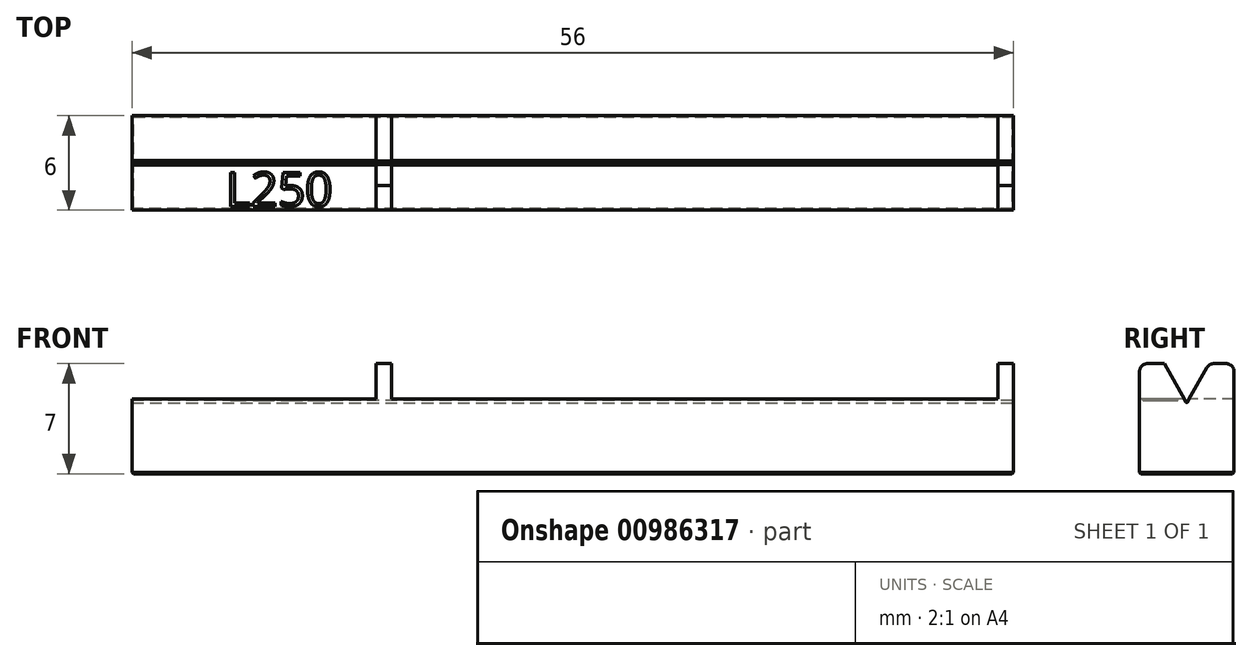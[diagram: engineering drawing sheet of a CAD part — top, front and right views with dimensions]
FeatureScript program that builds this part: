
annotation { "Feature Type Name" : "Feature", "Feature Type Description" : "" }
export const myFeature = defineFeature(function(context is Context, id is Id, definition is map)
    precondition{}
    {
        {
            var Q0;
            Q0=qCreatedBy(makeId("Top.planeOp"),FACE);
            var sketch = newSketch(context, id + "F0", { "sketchPlane" : qUnion([Q0])});
            skLineSegment(sketch, "E0.bottom", {"start": v(-28, 3) * mm, "end": v(28, 3) * mm});
            skLineSegment(sketch, "E0.top", {"start": v(-28, -3) * mm, "end": v(28, -3) * mm});
            skLineSegment(sketch, "E0.left", {"start": v(-28, 3) * mm, "end": v(-28, -3) * mm});
            skLineSegment(sketch, "E0.right", {"start": v(28, 3) * mm, "end": v(28, -3) * mm});
            skLineSegment(sketch, "E1", {"start": v(0, 9.05) * mm, "end": v(0, -9.2) * mm, "construction": true});
            skLineSegment(sketch, "E2", {"start": v(-9.84, 0) * mm, "end": v(11.26, 0) * mm, "construction": true});
            skSolve(sketch);
        }
        {
            var Q0;
            Q0 = qSketchRegion(id + "F0", true);
            extrude(context, id + "F1", {"entities" : qUnion([Q0]), "depth" : 7 * mm, "offsetDistance" : 25 * mm});
        }
        {
            var Q0;
            Q0=makeQuery(id+"F1.opExtrude","CAP_FACE",FACE,{"disambiguationData":[OSD([sQuery(id+"F0.wireOp",EDGE,"E0.bottom"),sQuery(id+"F0.wireOp",EDGE,"E0.top"),sQuery(id+"F0.wireOp",EDGE,"E0.left"),sQuery(id+"F0.wireOp",EDGE,"E0.right")])],"isStart":false});
            var sketch = newSketch(context, id + "F2", { "sketchPlane" : qUnion([Q0])});
            skLineSegment(sketch, "E3.bottom", {"start": v(-11.5, -3) * mm, "end": v(27, -3) * mm});
            skLineSegment(sketch, "E3.top", {"start": v(-11.5, 3) * mm, "end": v(27, 3) * mm});
            skLineSegment(sketch, "E3.left", {"start": v(-11.5, -3) * mm, "end": v(-11.5, 3) * mm});
            skLineSegment(sketch, "E3.right", {"start": v(27, -3) * mm, "end": v(27, 3) * mm});
            skLineSegment(sketch, "E4.bottom", {"start": v(-28, -3) * mm, "end": v(-12.5, -3) * mm});
            skLineSegment(sketch, "E4.top", {"start": v(-28, 3) * mm, "end": v(-12.5, 3) * mm});
            skLineSegment(sketch, "E4.left", {"start": v(-28, -3) * mm, "end": v(-28, 3) * mm});
            skLineSegment(sketch, "E4.right", {"start": v(-12.5, -3) * mm, "end": v(-12.5, 3) * mm});
            skSolve(sketch);
        }
        {
            var Q0;
            Q0 = qSketchRegion(id + "F2", true);
            extrude(context, id + "F3", {"entities" : qUnion([Q0]), "operationType" : NewBodyOperationType.REMOVE, "oppositeDirection" : true, "depth" : (7 - 4.76) * mm, "offsetDistance" : 25 * mm});
        }
        {
            var Q0;
            Q0=makeQuery(id+"F1.opExtrude","SWEPT_FACE",FACE,{"disambiguationData":[OSD([sQuery(id+"F0.wireOp",EDGE,"E0.right")])]});
            var sketch = newSketch(context, id + "F4", { "sketchPlane" : qUnion([Q0])});
            skLineSegment(sketch, "E5", {"start": v(-1.44, 7) * mm, "end": v(-0.1, 4.7) * mm});
            skLineSegment(sketch, "E6", {"start": v(1.44, 7) * mm, "end": v(-1.44, 7) * mm});
            skArc(sketch, "E7", {"start": v(-0.05, 4.55) * mm, "mid": v(0, 4.52) * mm, "end": v(0.05, 4.55) * mm});
            skLineSegment(sketch, "E8", {"start": v(-0.1, 4.7) * mm, "end": v(-0.05, 4.55) * mm});
            skLineSegment(sketch, "E9", {"start": v(0.05, 4.55) * mm, "end": v(0.1, 4.7) * mm});
            skLineSegment(sketch, "E10.trimOffspring", {"start": v(0.1, 4.7) * mm, "end": v(1.44, 7) * mm});
            skLineSegment(sketch, "E11", {"start": v(0, 7) * mm, "end": v(0, -0.68) * mm, "construction": true});
            skLineSegment(sketch, "E12", {"start": v(-0.05, 4.55) * mm, "end": v(0, 4.44) * mm, "construction": true});
            skLineSegment(sketch, "E13", {"start": v(0, 4.44) * mm, "end": v(0.05, 4.55) * mm, "construction": true});
            skSolve(sketch);
        }
        {
            var Q0;
            Q0 = qSketchRegion(id + "F4", true);
            extrude(context, id + "F5", {"entities" : qUnion([Q0]), "operationType" : NewBodyOperationType.REMOVE, "endBound" : BoundingType.THROUGH_ALL, "oppositeDirection" : true, "depth" : 25 * mm, "offsetDistance" : 25 * mm});
        }
        {
            var Q0;
            {var subQ0=sQuery(id+"F0.wireOp",EDGE,"E0.right");var subQ1=sQuery(id+"F0.wireOp",EDGE,"E0.top");Q0=makeQuery(id+"F3.boolean.opBoolean","SPLIT",EDGE,{"disambiguationData":[TD([makeQuery(id+"F1.opExtrude","SWEPT_FACE",FACE,{"disambiguationData":[OSD([subQ0])]})])],"derivedFrom":makeQuery(id+"F1.opExtrude","CAP_EDGE",EDGE,{"disambiguationData":[OSD([subQ1])],"isStart":false})});}
            var Q1;
            {var subQ0=sQuery(id+"F0.wireOp",EDGE,"E0.bottom");var subQ1=sQuery(id+"F0.wireOp",EDGE,"E0.right");Q1=makeQuery(id+"F3.boolean.opBoolean","SPLIT",EDGE,{"disambiguationData":[TD([makeQuery(id+"F1.opExtrude","SWEPT_FACE",FACE,{"disambiguationData":[OSD([subQ1])]})])],"derivedFrom":makeQuery(id+"F1.opExtrude","CAP_EDGE",EDGE,{"disambiguationData":[OSD([subQ0])],"isStart":false})});}
            var Q2;
            {var subQ0=sQuery(id+"F0.wireOp",EDGE,"E0.top");Q2=makeQuery(id+"F3.boolean.opBoolean","SPLIT",EDGE,{"disambiguationData":[TD([makeQuery(id+"F3.opExtrude","SWEPT_FACE",FACE,{"disambiguationData":[OSD([sQuery(id+"F2.wireOp",EDGE,"E3.left")])]})])],"derivedFrom":makeQuery(id+"F1.opExtrude","CAP_EDGE",EDGE,{"disambiguationData":[OSD([subQ0])],"isStart":false})});}
            var Q3;
            {var subQ0=sQuery(id+"F0.wireOp",EDGE,"E0.bottom");Q3=makeQuery(id+"F3.boolean.opBoolean","SPLIT",EDGE,{"disambiguationData":[TD([makeQuery(id+"F3.opExtrude","SWEPT_FACE",FACE,{"disambiguationData":[OSD([sQuery(id+"F2.wireOp",EDGE,"E3.left")])]})])],"derivedFrom":makeQuery(id+"F1.opExtrude","CAP_EDGE",EDGE,{"disambiguationData":[OSD([subQ0])],"isStart":false})});}
            var Q4;
            {var subQ0=sQuery(id+"F0.wireOp",EDGE,"E0.right");var subQ1=sQuery(id+"F4.wireOp",EDGE,"E10.trimOffspring");Q4=makeQuery(id+"F5.boolean.opBoolean","COPY",EDGE,{"disambiguationData":[TD([makeQuery(id+"F3.boolean.opBoolean","COPY",FACE,{"derivedFrom":makeQuery(id+"F3.opExtrude","SWEPT_FACE",FACE,{"disambiguationData":[OSD([sQuery(id+"F2.wireOp",EDGE,"E3.left")])]})})])],"derivedFrom":makeQuery(id+"F5.opExtrude","SWEPT_EDGE",EDGE,{"disambiguationData":[OSD([subQ0,sQuery(id+"F4.wireOp",EDGE,"E6"),subQ1])]})});}
            var Q5;
            {var subQ0=sQuery(id+"F0.wireOp",EDGE,"E0.right");var subQ1=sQuery(id+"F4.wireOp",EDGE,"E5");Q5=makeQuery(id+"F5.boolean.opBoolean","COPY",EDGE,{"disambiguationData":[TD([makeQuery(id+"F3.boolean.opBoolean","COPY",FACE,{"derivedFrom":makeQuery(id+"F3.opExtrude","SWEPT_FACE",FACE,{"disambiguationData":[OSD([sQuery(id+"F2.wireOp",EDGE,"E3.left")])]})})])],"derivedFrom":makeQuery(id+"F5.opExtrude","SWEPT_EDGE",EDGE,{"disambiguationData":[OSD([subQ0,subQ1,sQuery(id+"F4.wireOp",EDGE,"E6")])]})});}
            var Q6;
            {var subQ0=sQuery(id+"F0.wireOp",EDGE,"E0.right");var subQ1=sQuery(id+"F4.wireOp",EDGE,"E5");Q6=makeQuery(id+"F5.boolean.opBoolean","COPY",EDGE,{"disambiguationData":[TD([makeQuery(id+"F1.opExtrude","SWEPT_FACE",FACE,{"disambiguationData":[OSD([subQ0])]})])],"derivedFrom":makeQuery(id+"F5.opExtrude","SWEPT_EDGE",EDGE,{"disambiguationData":[OSD([subQ0,subQ1,sQuery(id+"F4.wireOp",EDGE,"E6")])]})});}
            var Q7;
            {var subQ0=sQuery(id+"F0.wireOp",EDGE,"E0.right");var subQ1=sQuery(id+"F4.wireOp",EDGE,"E10.trimOffspring");Q7=makeQuery(id+"F5.boolean.opBoolean","COPY",EDGE,{"disambiguationData":[TD([makeQuery(id+"F1.opExtrude","SWEPT_FACE",FACE,{"disambiguationData":[OSD([subQ0])]})])],"derivedFrom":makeQuery(id+"F5.opExtrude","SWEPT_EDGE",EDGE,{"disambiguationData":[OSD([subQ0,sQuery(id+"F4.wireOp",EDGE,"E6"),subQ1])]})});}
            fillet(context, id + "F6", {"entities" : qUnion([Q0, Q1, Q2, Q3, Q4, Q5, Q6, Q7]), "radius" : 0.5 * mm, "tangentPropagation" : true, "allowEdgeOverflow" : false});
        }
        {
            var Q0;
            Q0=makeQuery(id+"F1.opExtrude","CAP_EDGE",EDGE,{"disambiguationData":[OSD([sQuery(id+"F0.wireOp",EDGE,"E0.top")])],"isStart":true});
            var Q1;
            Q1=makeQuery(id+"F1.opExtrude","CAP_EDGE",EDGE,{"disambiguationData":[OSD([sQuery(id+"F0.wireOp",EDGE,"E0.right")])],"isStart":true});
            var Q2;
            Q2=makeQuery(id+"F1.opExtrude","CAP_EDGE",EDGE,{"disambiguationData":[OSD([sQuery(id+"F0.wireOp",EDGE,"E0.bottom")])],"isStart":true});
            var Q3;
            Q3=makeQuery(id+"F1.opExtrude","CAP_EDGE",EDGE,{"disambiguationData":[OSD([sQuery(id+"F0.wireOp",EDGE,"E0.left")])],"isStart":true});
            var Q4;
            {var subQ0=sQuery(id+"F2.wireOp",EDGE,"E4.left");Q4=makeQuery(id+"F5.boolean.opBoolean","SPLIT",EDGE,{"disambiguationData":[TD([makeQuery(id+"F1.opExtrude","SWEPT_FACE",FACE,{"disambiguationData":[OSD([sQuery(id+"F0.wireOp",EDGE,"E0.top")])]})])],"derivedFrom":makeQuery(id+"F3.boolean.opBoolean","COPY",EDGE,{"derivedFrom":makeQuery(id+"F3.opExtrude","CAP_EDGE",EDGE,{"disambiguationData":[OSD([subQ0])],"isStart":false})})});}
            var Q5;
            {var subQ0=sQuery(id+"F2.wireOp",EDGE,"E4.left");Q5=makeQuery(id+"F5.boolean.opBoolean","SPLIT",EDGE,{"disambiguationData":[TD([makeQuery(id+"F1.opExtrude","SWEPT_FACE",FACE,{"disambiguationData":[OSD([sQuery(id+"F0.wireOp",EDGE,"E0.bottom")])]})])],"derivedFrom":makeQuery(id+"F3.boolean.opBoolean","COPY",EDGE,{"derivedFrom":makeQuery(id+"F3.opExtrude","CAP_EDGE",EDGE,{"disambiguationData":[OSD([subQ0])],"isStart":false})})});}
            chamfer(context, id + "F7", {"entities" : qUnion([Q0, Q1, Q2, Q3, Q4, Q5]), "width" : 0.1 * mm, "tangentPropagation" : true});
        }
        {
            var Q0;
            {var subQ0=sQuery(id+"F2.wireOp",EDGE,"E4.right");Q0=makeQuery(id+"F5.boolean.opBoolean","SPLIT",FACE,{"disambiguationData":[TD([makeQuery(id+"F1.opExtrude","SWEPT_FACE",FACE,{"disambiguationData":[OSD([sQuery(id+"F0.wireOp",EDGE,"E0.top")])]})])],"derivedFrom":makeQuery(id+"F3.boolean.opBoolean","COPY",FACE,{"derivedFrom":makeQuery(id+"F3.opExtrude","CAP_FACE",FACE,{"disambiguationData":[OSD([sQuery(id+"F2.wireOp",EDGE,"E4.bottom"),sQuery(id+"F2.wireOp",EDGE,"E4.top"),sQuery(id+"F2.wireOp",EDGE,"E4.left"),subQ0])],"isStart":false})})});}
            var sketch = newSketch(context, id + "F8", { "sketchPlane" : qUnion([Q0])});
            skText(sketch, "E14", { "text": "L250", "fontName": "OpenSans-Regular.ttf"});
            const initialGuessF8  = {"E14": [-0.02203, -0.00276, 1, 0, 0.00218]};
            skSetInitialGuess(sketch, initialGuessF8);
            skSolve(sketch);
        }
        {
            var Q0;
            Q0 = qSketchRegion(id + "F8", true);
            extrude(context, id + "F9", {"entities" : qUnion([Q0]), "operationType" : NewBodyOperationType.REMOVE, "oppositeDirection" : true, "depth" : 0.1 * mm, "offsetDistance" : 25 * mm});
        }
    });
